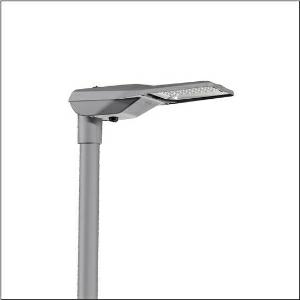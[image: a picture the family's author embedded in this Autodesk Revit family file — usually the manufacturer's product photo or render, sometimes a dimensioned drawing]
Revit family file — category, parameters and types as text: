
# Revit family: streetlight_sl_21_mini___stw1_0a_5xe2e43t08gb_b683
name_source: partatom
category: Lighting Fixtures
units: mm (PartAtom-declared; Revit-internal decimal feet)

## family parameters
Cut with Voids When Loaded = No
Host = Face
Light Source = No
Part Type = Normal
Room Calculation Point = No
Round Connector Dimension = Use Diameter
Shared = No

## types (1)
- --- (1 x LED, 6180 lm, 40.4 W, 4000K)
    Apparent Load = 40 VA
    CIE Flux Codes = 38 75 98 100 100
    Color Rendering = 70
    Color Temperature = 4000K
    Default Elevation = 1800 mm
    Description = Streetlight SL 21 mini, mast luminaire, primary light control with lens, of PMMA, primary optical cover: cover, of toughened safety glass, transparent, light distribution: STW1.0a, light emission: direct distribution, primary light characteristic: asymmetric, installation type: side-entry, post-top, LED, High Power LED, rated luminous flux: 6.180lm, luminous efficacy: 153lm/W, light colour: 740, colour temperature: 4000K, control gear: D4i, control: overheat protection, constant luminous flux control, time-dependent luminous flux control, flexible luminous flux parameterisation, pre-setting: logarithmic dimming characteristic, mains connection: 220..240V, AC, 50/60Hz, start of lifetime: 40W, end of service life: 41W, reduction: 19W, luminaire housing, of diecast aluminium, powder-coated, SITECO metallic grey (DB 702S), corrosivity category C5 high according to DIN EN ISO 12944, please order mast flange separately, inclination adjustable: 0°, 5°, 10°, 15°, sealing non-destructively replaceable, multi-level sealing system, length: 628mm, width: 235mm, height: 110mm, mast flange for spigot size: 42mm (side-entry): 5XC10008XM4, 60/48mm (side-entry/post-top): 5XC10108XM2, 76/60mm (side-entry/post-top): 5XC10108XM1, mounting height: 4..8m, Smart Interface below and above, protection rating (complete): IP66, insulation class (complete): insulation class II (safety insulation), certification: CE, ENEC, ENEC+, VDE, impact resistance: IK10, permissible operating ambient temperature for outdoor applications: -40..+50°C, standard-compliant lighting for roads and squares, packaging unit: 1 piece

Light Distribution: STW1.0a
    Height = 110 mm
    Lamp = 1 x LED
    Lamp Light Flux = 6180 lm
    Lamp Power = 40.4 W
    Lamp count = 1
    Length = 625 mm
    Luminous efficacy = 153 lm/W
    Manufacturer = Siteco
    ModVariant = No
    Model = 5XE2E43T08GB
    Number of Poles = 1
    OnlyDefault = Yes
    Power Factor = 1
    Product Name = Streetlight SL 21 mini | STW1.0a
    Product group = mast luminaire | pylon top
    ProductGroupID = 6100
    Protection Class = Protection class II
    Protection Degree = IP 66
    RLX_Detail_Level = 1
    RLX_Emergency_Light_Flux = 0 lm
    RLX_Emergency_Type = 0
    RLX_Emergency_Type_DB = No
    RlxData = <blob elided: 26361 chars, md5=4b03346e>
    Socket = socket
    Standby Power = 0 W
    System Light Flux = 6180 lm
    System Power = 40 W
    Type Comments = factory setting: luminous flux: 100 % | dim-lin: 254 | 812 mA
    Type Image = l_1003514.jpg
    URL = http://relux.com
    VarID = @adj_184723
    Voltage = 0 V
    Weight = 0.00 kg
    Width = 234 mm

## geometry (parser evidence)
native form markers: Blend x4, Sweep x12
no freeform markers — native parametric forms only
